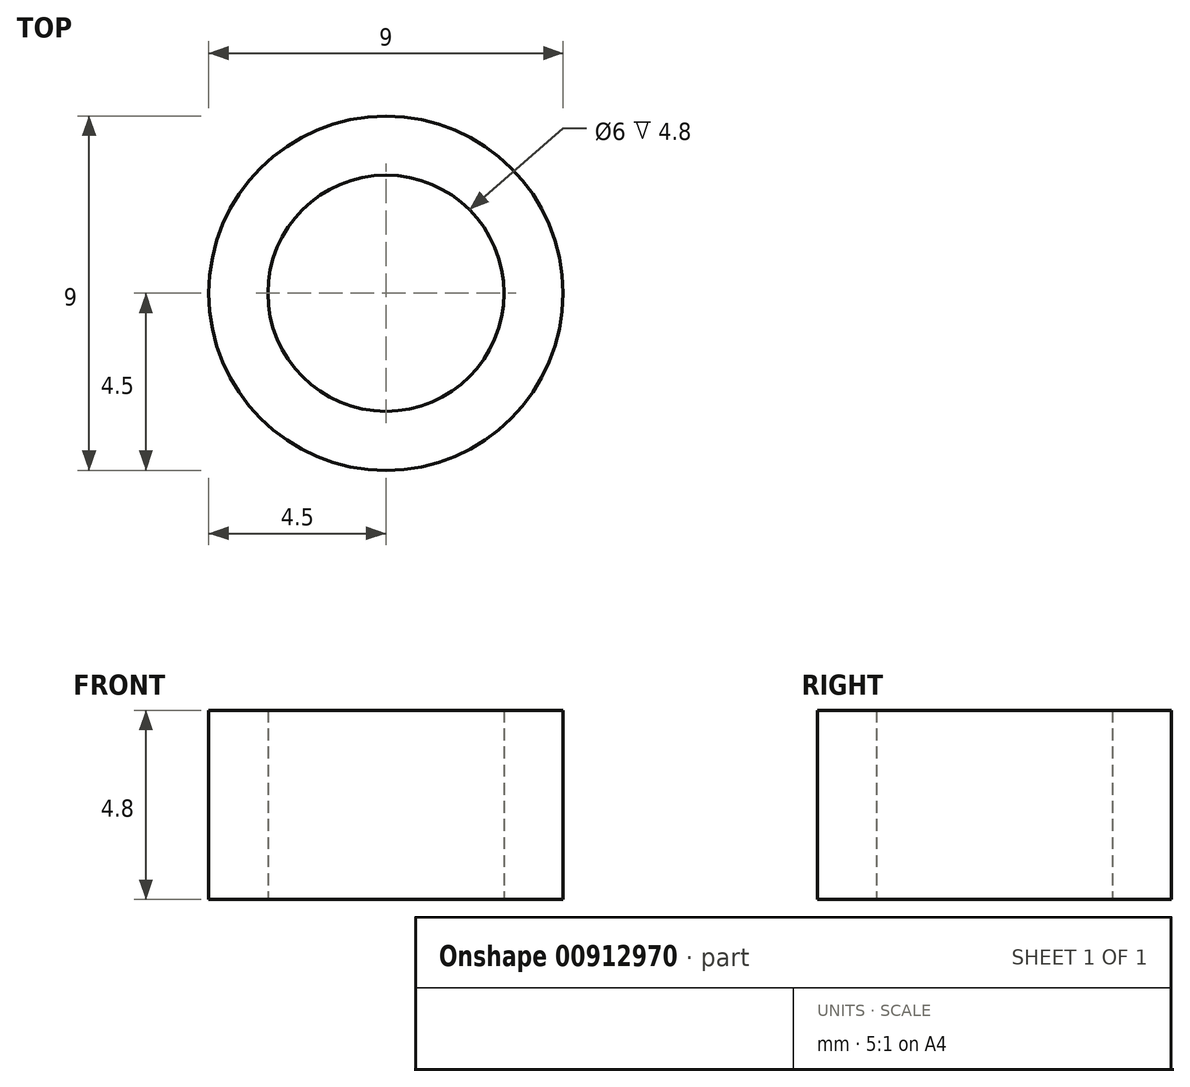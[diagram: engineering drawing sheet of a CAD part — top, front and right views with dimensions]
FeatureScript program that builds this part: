
annotation { "Feature Type Name" : "Feature", "Feature Type Description" : "" }
export const myFeature = defineFeature(function(context is Context, id is Id, definition is map)
    precondition{}
    {
        {
            var Q0;
            Q0=qCreatedBy(makeId("Top.planeOp"),FACE);
            var sketch = newSketch(context, id + "F0", { "sketchPlane" : qUnion([Q0])});
            skCircle(sketch, "E0", {"center": v(0, 0) * mm, "radius": 4.5 * mm});
            skCircle(sketch, "E1", {"center": v(0, 0) * mm, "radius": 3 * mm});
            skSolve(sketch);
        }
        {
            var Q0;
            Q0=makeQuery(id+"F0.imprint","IMPRINT",FACE,{"disambiguationData":[TD([[makeQuery(id+"F0.imprint","IMPRINT",EDGE,{"derivedFrom":sQuery(id+"F0.wireOp",EDGE,"E0")}),1.0]])]});
            extrude(context, id + "F1", {"entities" : qUnion([Q0]), "depth" : 4.8 * mm, "offsetDistance" : 25 * mm});
        }
    });
